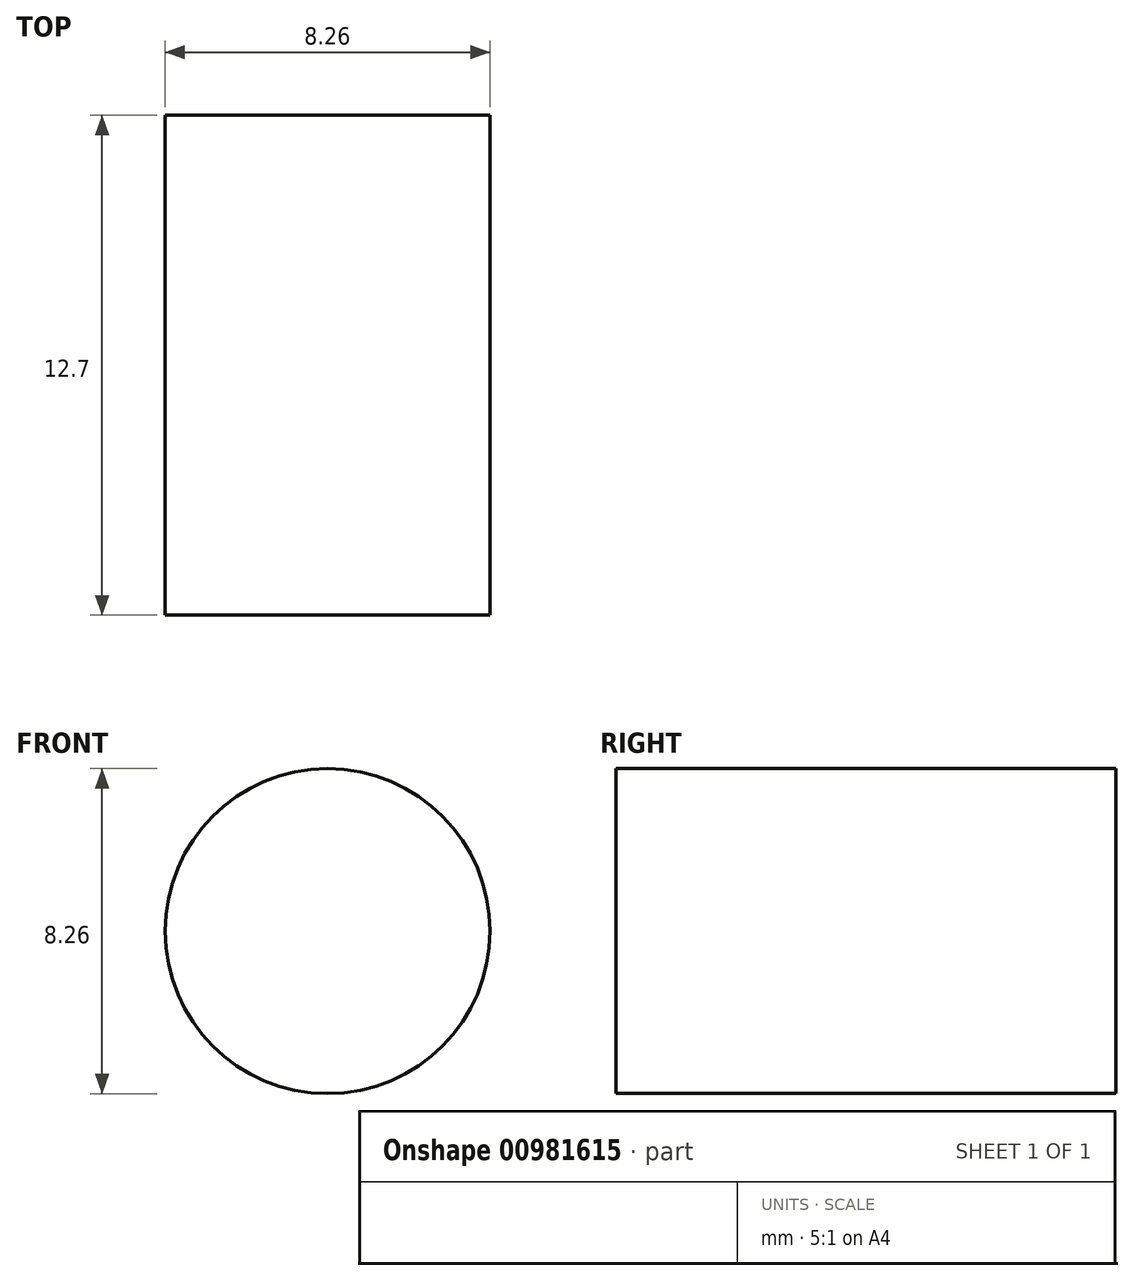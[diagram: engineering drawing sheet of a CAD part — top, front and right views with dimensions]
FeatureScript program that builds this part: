
annotation { "Feature Type Name" : "Feature", "Feature Type Description" : "" }
export const myFeature = defineFeature(function(context is Context, id is Id, definition is map)
    precondition{}
    {
        {
            var Q0;
            Q0=qCreatedBy(makeId("Front.planeOp"),FACE);
            var sketch = newSketch(context, id + "F0", { "sketchPlane" : qUnion([Q0])});
            skCircle(sketch, "E0", {"center": v(0, 0) * mm, "radius": 4.13 * mm});
            skSolve(sketch);
        }
        {
            var Q0;
            Q0 = qSketchRegion(id + "F0", true);
            extrude(context, id + "F1", {"entities" : qUnion([Q0]), "depth" : 12.7 * mm, "offsetDistance" : 25.4 * mm});
        }
    });
